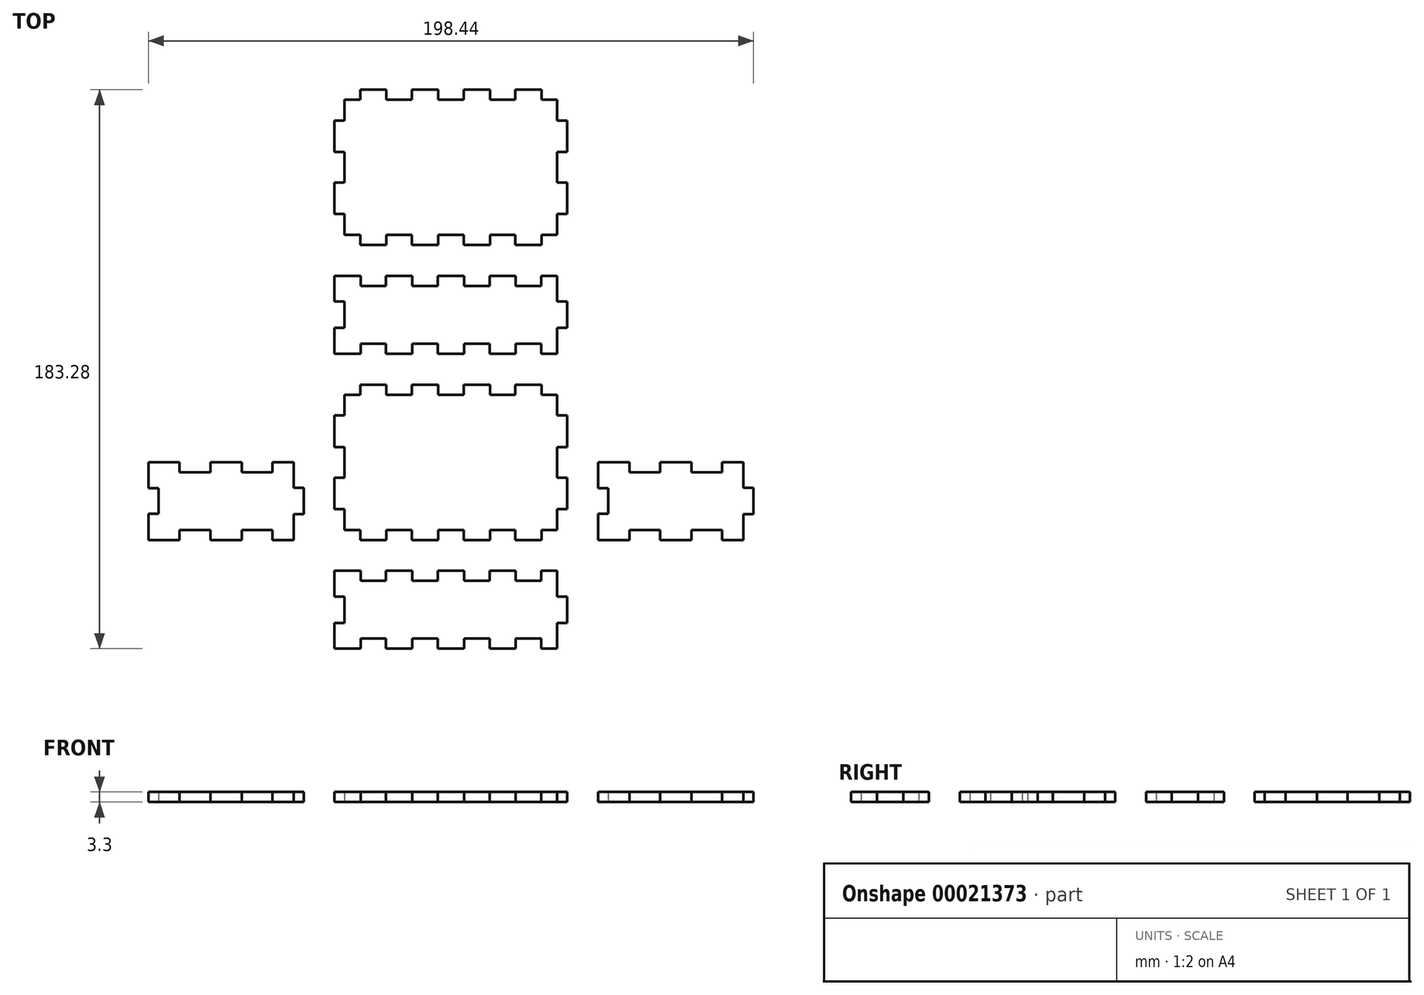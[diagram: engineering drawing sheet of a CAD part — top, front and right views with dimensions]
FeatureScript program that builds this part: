
annotation { "Feature Type Name" : "Feature", "Feature Type Description" : "" }
export const myFeature = defineFeature(function(context is Context, id is Id, definition is map)
    precondition{}
    {
        {
            var Q0;
            Q0=qCreatedBy(makeId("Top.planeOp"),FACE);
            var sketch = newSketch(context, id + "F0", { "sketchPlane" : qUnion([Q0])});
            skLineSegment(sketch, "E0", {"start": v(-38.16, -91.64) * mm, "end": v(-29.62, -91.64) * mm});
            skLineSegment(sketch, "E1", {"start": v(-29.62, -88.34) * mm, "end": v(-29.62, -91.64) * mm});
            skLineSegment(sketch, "E2", {"start": v(-29.62, -88.34) * mm, "end": v(-21.27, -88.34) * mm});
            skLineSegment(sketch, "E3", {"start": v(-21.27, -88.34) * mm, "end": v(-21.27, -91.64) * mm});
            skLineSegment(sketch, "E4", {"start": v(-21.27, -91.64) * mm, "end": v(-12.66, -91.64) * mm});
            skLineSegment(sketch, "E5", {"start": v(-12.66, -88.34) * mm, "end": v(-12.66, -91.64) * mm});
            skLineSegment(sketch, "E6", {"start": v(-12.66, -88.34) * mm, "end": v(-4.3, -88.34) * mm});
            skLineSegment(sketch, "E7", {"start": v(-4.3, -88.34) * mm, "end": v(-4.3, -91.64) * mm});
            skLineSegment(sketch, "E8", {"start": v(-4.3, -91.64) * mm, "end": v(4.3, -91.64) * mm});
            skLineSegment(sketch, "E9", {"start": v(4.3, -88.34) * mm, "end": v(4.3, -91.64) * mm});
            skLineSegment(sketch, "E10", {"start": v(4.3, -88.34) * mm, "end": v(12.66, -88.34) * mm});
            skLineSegment(sketch, "E11", {"start": v(12.66, -88.34) * mm, "end": v(12.66, -91.64) * mm});
            skLineSegment(sketch, "E12", {"start": v(12.66, -91.64) * mm, "end": v(21.27, -91.64) * mm});
            skLineSegment(sketch, "E13", {"start": v(21.27, -88.34) * mm, "end": v(21.27, -91.64) * mm});
            skLineSegment(sketch, "E14", {"start": v(21.27, -88.34) * mm, "end": v(29.62, -88.34) * mm});
            skLineSegment(sketch, "E15", {"start": v(29.62, -88.34) * mm, "end": v(29.62, -91.64) * mm});
            skLineSegment(sketch, "E16", {"start": v(29.62, -91.64) * mm, "end": v(34.86, -91.64) * mm});
            skLineSegment(sketch, "E17", {"start": v(-38.16, -66.12) * mm, "end": v(-29.62, -66.12) * mm});
            skLineSegment(sketch, "E18", {"start": v(-29.62, -66.12) * mm, "end": v(-29.62, -69.42) * mm});
            skLineSegment(sketch, "E19", {"start": v(-29.62, -69.42) * mm, "end": v(-21.27, -69.42) * mm});
            skLineSegment(sketch, "E20", {"start": v(-21.27, -66.12) * mm, "end": v(-21.27, -69.42) * mm});
            skLineSegment(sketch, "E21", {"start": v(-21.27, -66.12) * mm, "end": v(-12.66, -66.12) * mm});
            skLineSegment(sketch, "E22", {"start": v(-12.66, -66.12) * mm, "end": v(-12.66, -69.42) * mm});
            skLineSegment(sketch, "E23", {"start": v(-12.66, -69.42) * mm, "end": v(-4.3, -69.42) * mm});
            skLineSegment(sketch, "E24", {"start": v(-4.3, -66.12) * mm, "end": v(-4.3, -69.42) * mm});
            skLineSegment(sketch, "E25", {"start": v(-4.3, -66.12) * mm, "end": v(4.3, -66.12) * mm});
            skLineSegment(sketch, "E26", {"start": v(4.3, -66.12) * mm, "end": v(4.3, -69.42) * mm});
            skLineSegment(sketch, "E27", {"start": v(4.3, -69.42) * mm, "end": v(12.66, -69.42) * mm});
            skLineSegment(sketch, "E28", {"start": v(12.66, -66.12) * mm, "end": v(12.66, -69.42) * mm});
            skLineSegment(sketch, "E29", {"start": v(12.66, -66.12) * mm, "end": v(21.27, -66.12) * mm});
            skLineSegment(sketch, "E30", {"start": v(21.27, -66.12) * mm, "end": v(21.27, -69.42) * mm});
            skLineSegment(sketch, "E31", {"start": v(21.27, -69.42) * mm, "end": v(29.62, -69.42) * mm});
            skLineSegment(sketch, "E32", {"start": v(29.62, -66.12) * mm, "end": v(29.62, -69.42) * mm});
            skLineSegment(sketch, "E33", {"start": v(29.62, -66.12) * mm, "end": v(34.86, -66.12) * mm});
            skLineSegment(sketch, "E34", {"start": v(-38.16, -91.64) * mm, "end": v(-38.16, -83.2) * mm});
            skLineSegment(sketch, "E35", {"start": v(-34.86, -83.2) * mm, "end": v(-38.16, -83.2) * mm});
            skLineSegment(sketch, "E36", {"start": v(-34.86, -83.2) * mm, "end": v(-34.86, -74.56) * mm});
            skLineSegment(sketch, "E37", {"start": v(-34.86, -74.56) * mm, "end": v(-38.16, -74.56) * mm});
            skLineSegment(sketch, "E38", {"start": v(-38.16, -74.56) * mm, "end": v(-38.16, -66.12) * mm});
            skLineSegment(sketch, "E39", {"start": v(34.86, -91.64) * mm, "end": v(34.86, -83.2) * mm});
            skLineSegment(sketch, "E40", {"start": v(38.16, -83.2) * mm, "end": v(34.86, -83.2) * mm});
            skLineSegment(sketch, "E41", {"start": v(38.16, -83.2) * mm, "end": v(38.16, -74.56) * mm});
            skLineSegment(sketch, "E42", {"start": v(38.16, -74.56) * mm, "end": v(34.86, -74.56) * mm});
            skLineSegment(sketch, "E43", {"start": v(34.86, -74.56) * mm, "end": v(34.86, -66.12) * mm});
            skLineSegment(sketch, "E44", {"start": v(-99.22, -56) * mm, "end": v(-88.97, -56) * mm});
            skLineSegment(sketch, "E45", {"start": v(-88.97, -52.69) * mm, "end": v(-88.97, -56) * mm});
            skLineSegment(sketch, "E46", {"start": v(-88.97, -52.69) * mm, "end": v(-78.91, -52.69) * mm});
            skLineSegment(sketch, "E47", {"start": v(-78.91, -52.69) * mm, "end": v(-78.91, -56) * mm});
            skLineSegment(sketch, "E48", {"start": v(-78.91, -56) * mm, "end": v(-68.6, -56) * mm});
            skLineSegment(sketch, "E49", {"start": v(-68.6, -52.69) * mm, "end": v(-68.6, -56) * mm});
            skLineSegment(sketch, "E50", {"start": v(-68.6, -52.69) * mm, "end": v(-58.54, -52.69) * mm});
            skLineSegment(sketch, "E51", {"start": v(-58.54, -52.69) * mm, "end": v(-58.54, -56) * mm});
            skLineSegment(sketch, "E52", {"start": v(-58.54, -56) * mm, "end": v(-51.6, -56) * mm});
            skLineSegment(sketch, "E53", {"start": v(-99.22, -30.46) * mm, "end": v(-88.97, -30.46) * mm});
            skLineSegment(sketch, "E54", {"start": v(-88.97, -30.46) * mm, "end": v(-88.97, -33.77) * mm});
            skLineSegment(sketch, "E55", {"start": v(-88.97, -33.77) * mm, "end": v(-78.91, -33.77) * mm});
            skLineSegment(sketch, "E56", {"start": v(-78.91, -30.46) * mm, "end": v(-78.91, -33.77) * mm});
            skLineSegment(sketch, "E57", {"start": v(-78.91, -30.46) * mm, "end": v(-68.6, -30.46) * mm});
            skLineSegment(sketch, "E58", {"start": v(-68.6, -30.46) * mm, "end": v(-68.6, -33.77) * mm});
            skLineSegment(sketch, "E59", {"start": v(-68.6, -33.77) * mm, "end": v(-58.54, -33.77) * mm});
            skLineSegment(sketch, "E60", {"start": v(-58.54, -30.46) * mm, "end": v(-58.54, -33.77) * mm});
            skLineSegment(sketch, "E61", {"start": v(-58.54, -30.46) * mm, "end": v(-51.6, -30.46) * mm});
            skLineSegment(sketch, "E62", {"start": v(-99.22, -56) * mm, "end": v(-99.22, -47.42) * mm});
            skLineSegment(sketch, "E63", {"start": v(-95.92, -47.42) * mm, "end": v(-99.22, -47.42) * mm});
            skLineSegment(sketch, "E64", {"start": v(-95.92, -47.42) * mm, "end": v(-95.92, -39.04) * mm});
            skLineSegment(sketch, "E65", {"start": v(-95.92, -39.04) * mm, "end": v(-99.22, -39.04) * mm});
            skLineSegment(sketch, "E66", {"start": v(-99.22, -39.04) * mm, "end": v(-99.22, -30.46) * mm});
            skLineSegment(sketch, "E67", {"start": v(-51.6, -56) * mm, "end": v(-51.6, -47.54) * mm});
            skLineSegment(sketch, "E68", {"start": v(-48.3, -47.54) * mm, "end": v(-51.6, -47.54) * mm});
            skLineSegment(sketch, "E69", {"start": v(-48.3, -47.54) * mm, "end": v(-48.3, -38.9) * mm});
            skLineSegment(sketch, "E70", {"start": v(-48.3, -38.9) * mm, "end": v(-51.6, -38.9) * mm});
            skLineSegment(sketch, "E71", {"start": v(-51.6, -38.9) * mm, "end": v(-51.6, -30.46) * mm});
            skLineSegment(sketch, "E72", {"start": v(-34.86, -52.69) * mm, "end": v(-29.75, -52.69) * mm});
            skLineSegment(sketch, "E73", {"start": v(-29.75, -52.69) * mm, "end": v(-29.75, -56) * mm});
            skLineSegment(sketch, "E74", {"start": v(-29.75, -56) * mm, "end": v(-21.14, -56) * mm});
            skLineSegment(sketch, "E75", {"start": v(-21.14, -52.69) * mm, "end": v(-21.14, -56) * mm});
            skLineSegment(sketch, "E76", {"start": v(-21.14, -52.69) * mm, "end": v(-12.78, -52.69) * mm});
            skLineSegment(sketch, "E77", {"start": v(-12.78, -52.69) * mm, "end": v(-12.78, -56) * mm});
            skLineSegment(sketch, "E78", {"start": v(-12.78, -56) * mm, "end": v(-4.18, -56) * mm});
            skLineSegment(sketch, "E79", {"start": v(-4.18, -52.69) * mm, "end": v(-4.18, -56) * mm});
            skLineSegment(sketch, "E80", {"start": v(-4.18, -52.69) * mm, "end": v(4.18, -52.69) * mm});
            skLineSegment(sketch, "E81", {"start": v(4.18, -52.69) * mm, "end": v(4.18, -56) * mm});
            skLineSegment(sketch, "E82", {"start": v(4.18, -56) * mm, "end": v(12.78, -56) * mm});
            skLineSegment(sketch, "E83", {"start": v(12.78, -52.69) * mm, "end": v(12.78, -56) * mm});
            skLineSegment(sketch, "E84", {"start": v(12.78, -52.69) * mm, "end": v(21.14, -52.69) * mm});
            skLineSegment(sketch, "E85", {"start": v(21.14, -52.69) * mm, "end": v(21.14, -56) * mm});
            skLineSegment(sketch, "E86", {"start": v(21.14, -56) * mm, "end": v(29.75, -56) * mm});
            skLineSegment(sketch, "E87", {"start": v(29.75, -52.69) * mm, "end": v(29.75, -56) * mm});
            skLineSegment(sketch, "E88", {"start": v(29.75, -52.69) * mm, "end": v(34.86, -52.69) * mm});
            skLineSegment(sketch, "E89", {"start": v(-34.86, -8.37) * mm, "end": v(-29.75, -8.37) * mm});
            skLineSegment(sketch, "E90", {"start": v(-29.75, -5.06) * mm, "end": v(-29.75, -8.37) * mm});
            skLineSegment(sketch, "E91", {"start": v(-29.75, -5.06) * mm, "end": v(-21.14, -5.06) * mm});
            skLineSegment(sketch, "E92", {"start": v(-21.14, -5.06) * mm, "end": v(-21.14, -8.37) * mm});
            skLineSegment(sketch, "E93", {"start": v(-21.14, -8.37) * mm, "end": v(-12.78, -8.37) * mm});
            skLineSegment(sketch, "E94", {"start": v(-12.78, -5.06) * mm, "end": v(-12.78, -8.37) * mm});
            skLineSegment(sketch, "E95", {"start": v(-12.78, -5.06) * mm, "end": v(-4.18, -5.06) * mm});
            skLineSegment(sketch, "E96", {"start": v(-4.18, -5.06) * mm, "end": v(-4.18, -8.37) * mm});
            skLineSegment(sketch, "E97", {"start": v(-4.18, -8.37) * mm, "end": v(4.18, -8.37) * mm});
            skLineSegment(sketch, "E98", {"start": v(4.18, -5.06) * mm, "end": v(4.18, -8.37) * mm});
            skLineSegment(sketch, "E99", {"start": v(4.18, -5.06) * mm, "end": v(12.78, -5.06) * mm});
            skLineSegment(sketch, "E100", {"start": v(12.78, -5.06) * mm, "end": v(12.78, -8.37) * mm});
            skLineSegment(sketch, "E101", {"start": v(12.78, -8.37) * mm, "end": v(21.14, -8.37) * mm});
            skLineSegment(sketch, "E102", {"start": v(21.14, -5.06) * mm, "end": v(21.14, -8.37) * mm});
            skLineSegment(sketch, "E103", {"start": v(21.14, -5.06) * mm, "end": v(29.75, -5.06) * mm});
            skLineSegment(sketch, "E104", {"start": v(29.75, -5.06) * mm, "end": v(29.75, -8.37) * mm});
            skLineSegment(sketch, "E105", {"start": v(29.75, -8.37) * mm, "end": v(34.86, -8.37) * mm});
            skLineSegment(sketch, "E106", {"start": v(-34.86, -52.69) * mm, "end": v(-34.86, -45.87) * mm});
            skLineSegment(sketch, "E107", {"start": v(-34.86, -45.87) * mm, "end": v(-38.16, -45.87) * mm});
            skLineSegment(sketch, "E108", {"start": v(-38.16, -45.87) * mm, "end": v(-38.16, -35.56) * mm});
            skLineSegment(sketch, "E109", {"start": v(-34.86, -35.56) * mm, "end": v(-38.16, -35.56) * mm});
            skLineSegment(sketch, "E110", {"start": v(-34.86, -35.56) * mm, "end": v(-34.86, -25.5) * mm});
            skLineSegment(sketch, "E111", {"start": v(-34.86, -25.5) * mm, "end": v(-38.16, -25.5) * mm});
            skLineSegment(sketch, "E112", {"start": v(-38.16, -25.5) * mm, "end": v(-38.16, -15.19) * mm});
            skLineSegment(sketch, "E113", {"start": v(-34.86, -15.19) * mm, "end": v(-38.16, -15.19) * mm});
            skLineSegment(sketch, "E114", {"start": v(-34.86, -15.19) * mm, "end": v(-34.86, -8.37) * mm});
            skLineSegment(sketch, "E115", {"start": v(34.86, -52.69) * mm, "end": v(34.86, -45.87) * mm});
            skLineSegment(sketch, "E116", {"start": v(38.16, -45.87) * mm, "end": v(34.86, -45.87) * mm});
            skLineSegment(sketch, "E117", {"start": v(38.16, -45.87) * mm, "end": v(38.16, -35.56) * mm});
            skLineSegment(sketch, "E118", {"start": v(38.16, -35.56) * mm, "end": v(34.86, -35.56) * mm});
            skLineSegment(sketch, "E119", {"start": v(34.86, -35.56) * mm, "end": v(34.86, -25.5) * mm});
            skLineSegment(sketch, "E120", {"start": v(38.16, -25.5) * mm, "end": v(34.86, -25.5) * mm});
            skLineSegment(sketch, "E121", {"start": v(38.16, -25.5) * mm, "end": v(38.16, -15.19) * mm});
            skLineSegment(sketch, "E122", {"start": v(38.16, -15.19) * mm, "end": v(34.86, -15.19) * mm});
            skLineSegment(sketch, "E123", {"start": v(34.86, -15.19) * mm, "end": v(34.86, -8.37) * mm});
            skLineSegment(sketch, "E124", {"start": v(48.3, -56) * mm, "end": v(58.54, -56) * mm});
            skLineSegment(sketch, "E125", {"start": v(58.54, -52.69) * mm, "end": v(58.54, -56) * mm});
            skLineSegment(sketch, "E126", {"start": v(58.54, -52.69) * mm, "end": v(68.6, -52.69) * mm});
            skLineSegment(sketch, "E127", {"start": v(68.6, -52.69) * mm, "end": v(68.6, -56) * mm});
            skLineSegment(sketch, "E128", {"start": v(68.6, -56) * mm, "end": v(78.91, -56) * mm});
            skLineSegment(sketch, "E129", {"start": v(78.91, -52.69) * mm, "end": v(78.91, -56) * mm});
            skLineSegment(sketch, "E130", {"start": v(78.91, -52.69) * mm, "end": v(88.97, -52.69) * mm});
            skLineSegment(sketch, "E131", {"start": v(88.97, -52.69) * mm, "end": v(88.97, -56) * mm});
            skLineSegment(sketch, "E132", {"start": v(88.97, -56) * mm, "end": v(95.92, -56) * mm});
            skLineSegment(sketch, "E133", {"start": v(48.3, -30.46) * mm, "end": v(58.54, -30.46) * mm});
            skLineSegment(sketch, "E134", {"start": v(58.54, -30.46) * mm, "end": v(58.54, -33.77) * mm});
            skLineSegment(sketch, "E135", {"start": v(58.54, -33.77) * mm, "end": v(68.6, -33.77) * mm});
            skLineSegment(sketch, "E136", {"start": v(68.6, -30.46) * mm, "end": v(68.6, -33.77) * mm});
            skLineSegment(sketch, "E137", {"start": v(68.6, -30.46) * mm, "end": v(78.91, -30.46) * mm});
            skLineSegment(sketch, "E138", {"start": v(78.91, -30.46) * mm, "end": v(78.91, -33.77) * mm});
            skLineSegment(sketch, "E139", {"start": v(78.91, -33.77) * mm, "end": v(88.97, -33.77) * mm});
            skLineSegment(sketch, "E140", {"start": v(88.97, -30.46) * mm, "end": v(88.97, -33.77) * mm});
            skLineSegment(sketch, "E141", {"start": v(88.97, -30.46) * mm, "end": v(95.92, -30.46) * mm});
            skLineSegment(sketch, "E142", {"start": v(48.3, -56) * mm, "end": v(48.3, -47.42) * mm});
            skLineSegment(sketch, "E143", {"start": v(51.6, -47.42) * mm, "end": v(48.3, -47.42) * mm});
            skLineSegment(sketch, "E144", {"start": v(51.6, -47.42) * mm, "end": v(51.6, -39.04) * mm});
            skLineSegment(sketch, "E145", {"start": v(51.6, -39.04) * mm, "end": v(48.3, -39.04) * mm});
            skLineSegment(sketch, "E146", {"start": v(48.3, -39.04) * mm, "end": v(48.3, -30.46) * mm});
            skLineSegment(sketch, "E147", {"start": v(95.92, -56) * mm, "end": v(95.92, -47.54) * mm});
            skLineSegment(sketch, "E148", {"start": v(99.22, -47.54) * mm, "end": v(95.92, -47.54) * mm});
            skLineSegment(sketch, "E149", {"start": v(99.22, -47.54) * mm, "end": v(99.22, -38.9) * mm});
            skLineSegment(sketch, "E150", {"start": v(99.22, -38.9) * mm, "end": v(95.92, -38.9) * mm});
            skLineSegment(sketch, "E151", {"start": v(95.92, -38.9) * mm, "end": v(95.92, -30.46) * mm});
            skLineSegment(sketch, "E152", {"start": v(-38.16, 5.06) * mm, "end": v(-29.62, 5.06) * mm});
            skLineSegment(sketch, "E153", {"start": v(-29.62, 8.37) * mm, "end": v(-29.62, 5.06) * mm});
            skLineSegment(sketch, "E154", {"start": v(-29.62, 8.37) * mm, "end": v(-21.27, 8.37) * mm});
            skLineSegment(sketch, "E155", {"start": v(-21.27, 8.37) * mm, "end": v(-21.27, 5.06) * mm});
            skLineSegment(sketch, "E156", {"start": v(-21.27, 5.06) * mm, "end": v(-12.66, 5.06) * mm});
            skLineSegment(sketch, "E157", {"start": v(-12.66, 8.37) * mm, "end": v(-12.66, 5.06) * mm});
            skLineSegment(sketch, "E158", {"start": v(-12.66, 8.37) * mm, "end": v(-4.3, 8.37) * mm});
            skLineSegment(sketch, "E159", {"start": v(-4.3, 8.37) * mm, "end": v(-4.3, 5.06) * mm});
            skLineSegment(sketch, "E160", {"start": v(-4.3, 5.06) * mm, "end": v(4.3, 5.06) * mm});
            skLineSegment(sketch, "E161", {"start": v(4.3, 8.37) * mm, "end": v(4.3, 5.06) * mm});
            skLineSegment(sketch, "E162", {"start": v(4.3, 8.37) * mm, "end": v(12.66, 8.37) * mm});
            skLineSegment(sketch, "E163", {"start": v(12.66, 8.37) * mm, "end": v(12.66, 5.06) * mm});
            skLineSegment(sketch, "E164", {"start": v(12.66, 5.06) * mm, "end": v(21.27, 5.06) * mm});
            skLineSegment(sketch, "E165", {"start": v(21.27, 8.37) * mm, "end": v(21.27, 5.06) * mm});
            skLineSegment(sketch, "E166", {"start": v(21.27, 8.37) * mm, "end": v(29.62, 8.37) * mm});
            skLineSegment(sketch, "E167", {"start": v(29.62, 8.37) * mm, "end": v(29.62, 5.06) * mm});
            skLineSegment(sketch, "E168", {"start": v(29.62, 5.06) * mm, "end": v(34.86, 5.06) * mm});
            skLineSegment(sketch, "E169", {"start": v(-38.16, 30.6) * mm, "end": v(-29.62, 30.6) * mm});
            skLineSegment(sketch, "E170", {"start": v(-29.62, 30.6) * mm, "end": v(-29.62, 27.29) * mm});
            skLineSegment(sketch, "E171", {"start": v(-29.62, 27.29) * mm, "end": v(-21.27, 27.29) * mm});
            skLineSegment(sketch, "E172", {"start": v(-21.27, 30.6) * mm, "end": v(-21.27, 27.29) * mm});
            skLineSegment(sketch, "E173", {"start": v(-21.27, 30.6) * mm, "end": v(-12.66, 30.6) * mm});
            skLineSegment(sketch, "E174", {"start": v(-12.66, 30.6) * mm, "end": v(-12.66, 27.29) * mm});
            skLineSegment(sketch, "E175", {"start": v(-12.66, 27.29) * mm, "end": v(-4.3, 27.29) * mm});
            skLineSegment(sketch, "E176", {"start": v(-4.3, 30.6) * mm, "end": v(-4.3, 27.29) * mm});
            skLineSegment(sketch, "E177", {"start": v(-4.3, 30.6) * mm, "end": v(4.3, 30.6) * mm});
            skLineSegment(sketch, "E178", {"start": v(4.3, 30.6) * mm, "end": v(4.3, 27.29) * mm});
            skLineSegment(sketch, "E179", {"start": v(4.3, 27.29) * mm, "end": v(12.66, 27.29) * mm});
            skLineSegment(sketch, "E180", {"start": v(12.66, 30.6) * mm, "end": v(12.66, 27.29) * mm});
            skLineSegment(sketch, "E181", {"start": v(12.66, 30.6) * mm, "end": v(21.27, 30.6) * mm});
            skLineSegment(sketch, "E182", {"start": v(21.27, 30.6) * mm, "end": v(21.27, 27.29) * mm});
            skLineSegment(sketch, "E183", {"start": v(21.27, 27.29) * mm, "end": v(29.62, 27.29) * mm});
            skLineSegment(sketch, "E184", {"start": v(29.62, 30.6) * mm, "end": v(29.62, 27.29) * mm});
            skLineSegment(sketch, "E185", {"start": v(29.62, 30.6) * mm, "end": v(34.86, 30.6) * mm});
            skLineSegment(sketch, "E186", {"start": v(-38.16, 5.06) * mm, "end": v(-38.16, 13.5) * mm});
            skLineSegment(sketch, "E187", {"start": v(-34.86, 13.5) * mm, "end": v(-38.16, 13.5) * mm});
            skLineSegment(sketch, "E188", {"start": v(-34.86, 13.5) * mm, "end": v(-34.86, 22.15) * mm});
            skLineSegment(sketch, "E189", {"start": v(-34.86, 22.15) * mm, "end": v(-38.16, 22.15) * mm});
            skLineSegment(sketch, "E190", {"start": v(-38.16, 22.15) * mm, "end": v(-38.16, 30.6) * mm});
            skLineSegment(sketch, "E191", {"start": v(34.86, 5.06) * mm, "end": v(34.86, 13.5) * mm});
            skLineSegment(sketch, "E192", {"start": v(38.16, 13.5) * mm, "end": v(34.86, 13.5) * mm});
            skLineSegment(sketch, "E193", {"start": v(38.16, 13.5) * mm, "end": v(38.16, 22.15) * mm});
            skLineSegment(sketch, "E194", {"start": v(38.16, 22.15) * mm, "end": v(34.86, 22.15) * mm});
            skLineSegment(sketch, "E195", {"start": v(34.86, 22.15) * mm, "end": v(34.86, 30.6) * mm});
            skLineSegment(sketch, "E196", {"start": v(-34.86, 44.02) * mm, "end": v(-29.75, 44.02) * mm});
            skLineSegment(sketch, "E197", {"start": v(-29.75, 44.02) * mm, "end": v(-29.75, 40.72) * mm});
            skLineSegment(sketch, "E198", {"start": v(-29.75, 40.72) * mm, "end": v(-21.14, 40.72) * mm});
            skLineSegment(sketch, "E199", {"start": v(-21.14, 44.02) * mm, "end": v(-21.14, 40.72) * mm});
            skLineSegment(sketch, "E200", {"start": v(-21.14, 44.02) * mm, "end": v(-12.78, 44.02) * mm});
            skLineSegment(sketch, "E201", {"start": v(-12.78, 44.02) * mm, "end": v(-12.78, 40.72) * mm});
            skLineSegment(sketch, "E202", {"start": v(-12.78, 40.72) * mm, "end": v(-4.18, 40.72) * mm});
            skLineSegment(sketch, "E203", {"start": v(-4.18, 44.02) * mm, "end": v(-4.18, 40.72) * mm});
            skLineSegment(sketch, "E204", {"start": v(-4.18, 44.02) * mm, "end": v(4.18, 44.02) * mm});
            skLineSegment(sketch, "E205", {"start": v(4.18, 44.02) * mm, "end": v(4.18, 40.72) * mm});
            skLineSegment(sketch, "E206", {"start": v(4.18, 40.72) * mm, "end": v(12.78, 40.72) * mm});
            skLineSegment(sketch, "E207", {"start": v(12.78, 44.02) * mm, "end": v(12.78, 40.72) * mm});
            skLineSegment(sketch, "E208", {"start": v(12.78, 44.02) * mm, "end": v(21.14, 44.02) * mm});
            skLineSegment(sketch, "E209", {"start": v(21.14, 44.02) * mm, "end": v(21.14, 40.72) * mm});
            skLineSegment(sketch, "E210", {"start": v(21.14, 40.72) * mm, "end": v(29.75, 40.72) * mm});
            skLineSegment(sketch, "E211", {"start": v(29.75, 44.02) * mm, "end": v(29.75, 40.72) * mm});
            skLineSegment(sketch, "E212", {"start": v(29.75, 44.02) * mm, "end": v(34.86, 44.02) * mm});
            skLineSegment(sketch, "E213", {"start": v(-34.86, 88.34) * mm, "end": v(-29.75, 88.34) * mm});
            skLineSegment(sketch, "E214", {"start": v(-29.75, 91.64) * mm, "end": v(-29.75, 88.34) * mm});
            skLineSegment(sketch, "E215", {"start": v(-29.75, 91.64) * mm, "end": v(-21.14, 91.64) * mm});
            skLineSegment(sketch, "E216", {"start": v(-21.14, 91.64) * mm, "end": v(-21.14, 88.34) * mm});
            skLineSegment(sketch, "E217", {"start": v(-21.14, 88.34) * mm, "end": v(-12.78, 88.34) * mm});
            skLineSegment(sketch, "E218", {"start": v(-12.78, 91.64) * mm, "end": v(-12.78, 88.34) * mm});
            skLineSegment(sketch, "E219", {"start": v(-12.78, 91.64) * mm, "end": v(-4.18, 91.64) * mm});
            skLineSegment(sketch, "E220", {"start": v(-4.18, 91.64) * mm, "end": v(-4.18, 88.34) * mm});
            skLineSegment(sketch, "E221", {"start": v(-4.18, 88.34) * mm, "end": v(4.18, 88.34) * mm});
            skLineSegment(sketch, "E222", {"start": v(4.18, 91.64) * mm, "end": v(4.18, 88.34) * mm});
            skLineSegment(sketch, "E223", {"start": v(4.18, 91.64) * mm, "end": v(12.78, 91.64) * mm});
            skLineSegment(sketch, "E224", {"start": v(12.78, 91.64) * mm, "end": v(12.78, 88.34) * mm});
            skLineSegment(sketch, "E225", {"start": v(12.78, 88.34) * mm, "end": v(21.14, 88.34) * mm});
            skLineSegment(sketch, "E226", {"start": v(21.14, 91.64) * mm, "end": v(21.14, 88.34) * mm});
            skLineSegment(sketch, "E227", {"start": v(21.14, 91.64) * mm, "end": v(29.75, 91.64) * mm});
            skLineSegment(sketch, "E228", {"start": v(29.75, 91.64) * mm, "end": v(29.75, 88.34) * mm});
            skLineSegment(sketch, "E229", {"start": v(29.75, 88.34) * mm, "end": v(34.86, 88.34) * mm});
            skLineSegment(sketch, "E230", {"start": v(-34.86, 44.02) * mm, "end": v(-34.86, 50.84) * mm});
            skLineSegment(sketch, "E231", {"start": v(-34.86, 50.84) * mm, "end": v(-38.16, 50.84) * mm});
            skLineSegment(sketch, "E232", {"start": v(-38.16, 50.84) * mm, "end": v(-38.16, 61.15) * mm});
            skLineSegment(sketch, "E233", {"start": v(-34.86, 61.15) * mm, "end": v(-38.16, 61.15) * mm});
            skLineSegment(sketch, "E234", {"start": v(-34.86, 61.15) * mm, "end": v(-34.86, 71.21) * mm});
            skLineSegment(sketch, "E235", {"start": v(-34.86, 71.21) * mm, "end": v(-38.16, 71.21) * mm});
            skLineSegment(sketch, "E236", {"start": v(-38.16, 71.21) * mm, "end": v(-38.16, 81.52) * mm});
            skLineSegment(sketch, "E237", {"start": v(-34.86, 81.52) * mm, "end": v(-38.16, 81.52) * mm});
            skLineSegment(sketch, "E238", {"start": v(-34.86, 81.52) * mm, "end": v(-34.86, 88.34) * mm});
            skLineSegment(sketch, "E239", {"start": v(34.86, 44.02) * mm, "end": v(34.86, 50.84) * mm});
            skLineSegment(sketch, "E240", {"start": v(38.16, 50.84) * mm, "end": v(34.86, 50.84) * mm});
            skLineSegment(sketch, "E241", {"start": v(38.16, 50.84) * mm, "end": v(38.16, 61.15) * mm});
            skLineSegment(sketch, "E242", {"start": v(38.16, 61.15) * mm, "end": v(34.86, 61.15) * mm});
            skLineSegment(sketch, "E243", {"start": v(34.86, 61.15) * mm, "end": v(34.86, 71.21) * mm});
            skLineSegment(sketch, "E244", {"start": v(38.16, 71.21) * mm, "end": v(34.86, 71.21) * mm});
            skLineSegment(sketch, "E245", {"start": v(38.16, 71.21) * mm, "end": v(38.16, 81.52) * mm});
            skLineSegment(sketch, "E246", {"start": v(38.16, 81.52) * mm, "end": v(34.86, 81.52) * mm});
            skLineSegment(sketch, "E247", {"start": v(34.86, 81.52) * mm, "end": v(34.86, 88.34) * mm});
            skSolve(sketch);
        }
        {
            var Q0;
            Q0 = qSketchRegion(id + "F0", true);
            extrude(context, id + "F1", {"entities" : qUnion([Q0]), "depth" : 3.3 * mm});
        }
    });
